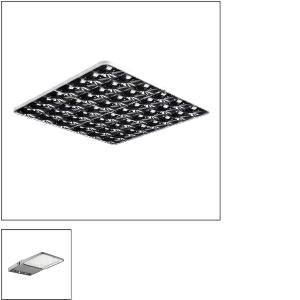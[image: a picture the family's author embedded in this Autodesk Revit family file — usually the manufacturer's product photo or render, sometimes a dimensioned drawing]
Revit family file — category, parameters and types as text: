
# Revit family: siteco_mirrortec_r__indoor___rs05_5nw14091qb_062b
name_source: partatom
category: Lighting Fixtures
units: mm (PartAtom-declared; Revit-internal decimal feet)

## family parameters
Cut with Voids When Loaded = No
Host = Face
Light Source = No
Part Type = Normal
Room Calculation Point = No
Round Connector Dimension = Use Diameter
Shared = No

## types (1)
- 5XA7682G2H2AC (1 x LED, 33820 lm, 305.7 W, 4000K)
    Apparent Load = 306 VA
    CIE Flux Codes = 47 83 98 55 100
    Color Rendering = 70
    Color Temperature = 4000K
    Default Elevation = 1800 mm
    Description = secondary reflector, for Siteco Mirrortec® Indoor, ball-and-socket joint pendant suspension, housing, square, of aluminium, coated, metallic grey (RAL 9006), fresnel reflector 100, of PMMA, aluminized, highly specular, light point resolution, fresnel structure, length: 900 mm, width: 900 mm

Light Distribution: RS05
    Height = 502 mm
    Lamp = 1 x LED
    Lamp Light Flux = 33820 lm
    Lamp Power = 305.7 W
    Lamp count = 1
    Length = 919 mm
    Luminous efficacy = 111 lm/W
    Manufacturer = Siteco
    ModVariant = No
    Model = 5NW14091QB
    Mounting Place = Ceiling
    Mounting Type = Pendant
    Number of Poles = 1
    OnlyDefault = Yes
    Power Factor = 1
    Product Name = Siteco Mirrortec® Indoor | RS05
    Product group = secondary reflector
    ProductGroupID = 908
    Protection Class = Protection class II
    Protection Degree = IP 66
    RLX_Detail_Level = 1
    RLX_Emergency_Light_Flux = 0 lm
    RLX_Emergency_Type = 0
    RLX_Emergency_Type_DB = No
    RlxData = <blob elided: 104453 chars, md5=f6fd1ac7>
    Socket = socket
    Standby Power = 0 W
    System Light Flux = 33820 lm
    System Power = 306 W
    Type Comments = Floodlight FL 20 midi, floodlight, primary light control with lens, of plastic, primary optical cover: protective disc, of toughened safety glass, transparent, light distribution: RS05, light emission: direct distribution, primary light characteristic: rotationally symmetric, installation type: surface-mounted, LED, High Power LED, rated luminous flux: 38.380lm, luminous efficacy: 126lm/W, light colour: 740, colour temperature: 4000K, control gear: ECG Plus, control: overheat protection, power reduction, digital communication interface, time-dependent luminous flux control, flexible luminous flux parameterisation, electronic power reduction, with terminal, 10-pole, max. 2.5mm², mains connection: 220..240V, AC, 50/60Hz, rated input power: 306W, LED unit, of diecast aluminium, powder-coated, Siteco® metallic grey (DB 702S), corrosivity category C5 mid according to DIN EN ISO 12944, length: 731mm, width: 450mm, height: 76mm, housing frame, of diecast aluminium, powder-coated, Siteco® metallic grey (DB 702S), wall fastening, DALI, protection rating (complete): IP66, insulation class (complete): insulation class II (safety insulation), certification: CE, ENEC, VDE, protection symbol: D, permissible operating ambient temperature: -40..+40°C, permissible operating ambient temperature for outdoor applications: -40..+50°C, standard: DIN EN 12944, packaging unit: 1 piece

individual setting: distance floodlight mirror = 2,5m / reflector tilt = 5°
    Type Image = l_577132_1005944.jpg
    URL = http://relux.com
    VarID = 5xa7682g2h2ac@adj_135717
    Voltage = 0 V
    Weight = 0.00 kg
    Width = 919 mm

## geometry (parser evidence)
native form markers: Blend x4, Sweep x11
no freeform markers — native parametric forms only
